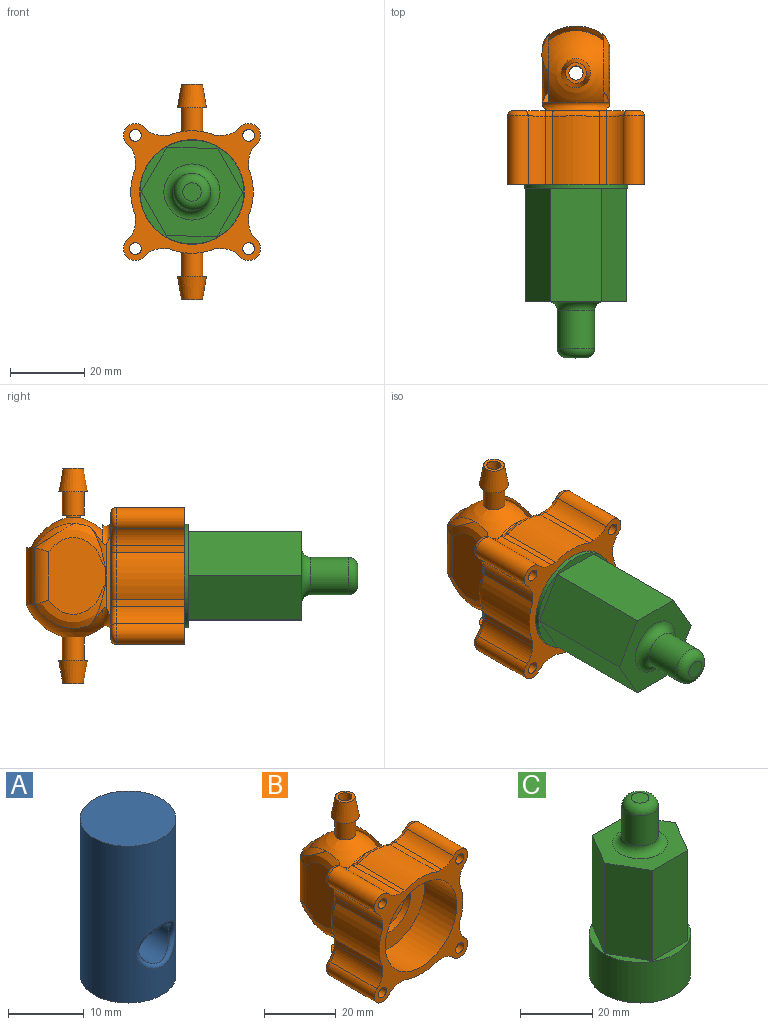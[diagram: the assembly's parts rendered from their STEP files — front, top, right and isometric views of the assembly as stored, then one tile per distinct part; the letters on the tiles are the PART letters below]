
ASSEMBLY  parts=3 mates=2
PART A: 6 faces, bbox 12.7x12.7x25.4 mm
  f0: cylinder r=6.35mm len=25.4mm, axis (0,0,-1), area 929.3mm2, adj f1,f2,f4,f5
  f1: plane 12.7x12.7mm, normal (0,0,1), area 126.7mm2, adj f0
  f2: plane 12.7x12.7mm, normal (0,0,-1), area 126.7mm2, adj f0
  f3: cylinder r=2.92mm len=11.68mm, axis (0,-1,0), area 194.6mm2, adj f4,f5
  f4: bspline ~7.46x6.86mm, area 19.4mm2, adj f0,f3
  f5: bspline ~7.46x6.86mm, area 19.4mm2, adj f0,f3
PART B: 95 faces, bbox 37.6x42.9x58.4 mm
  f0: cylinder r=16.51mm len=18.42mm, axis (0,-1,0), area 240.1mm2, adj f54,f56,f74,f94
  f1: cylinder r=16.51mm len=18.42mm, axis (0,-1,0), area 240.1mm2, adj f46,f52,f86,f94
  f2: cylinder r=16.51mm len=18.42mm, axis (0,-1,0), area 240.1mm2, adj f48,f58,f73,f94
  f3: cylinder r=11.43mm len=15.24mm, axis (0,0,-1), area 31.2mm2, adj f10,f11,f12,f13,f31,f33
  f4: cylinder r=11.43mm len=15.24mm, axis (0,0,-1), area 31.2mm2, adj f10,f11,f12,f13,f31,f35
  f5: cylinder r=11.43mm len=15.24mm, axis (0,0,-1), area 243.1mm2, adj f10,f11,f33,f35
  f6: revolved ~25.4x25.4mm, area 358.1mm2, adj f7,f19,f36,f37,f42,f43,f92
  f7: cylinder r=12.7mm len=15.24mm, axis (0,0,-1), area 238.7mm2, adj f6,f9,f38,f40
  f8: cylinder r=12.7mm len=24.07mm, axis (0,0,-1), area 39.5mm2, adj f25,f43,f92,f93
  f9: revolved ~25.4x25.4mm, area 358.2mm2, adj f7,f20,f37,f39,f41,f43,f93
  f10: revolved ~22.86x22.86mm, area 394.4mm2, adj f3,f4,f5,f12,f24,f33,f35
  f11: revolved ~22.86x22.86mm, area 394.4mm2, adj f3,f4,f5,f13,f15,f33,f35
  f12: plane 10.48x5.92mm, normal (0,1,0), area 35.4mm2, adj f3,f4,f10,f31
  f13: plane 10.48x5.92mm, normal (0,1,0), area 35.4mm2, adj f3,f4,f11,f31
  f14: cylinder r=12.7mm len=24.07mm, axis (0,0,-1), area 39.5mm2, adj f25,f37,f92,f93
  f15: cylinder r=1.91mm len=13.34mm, axis (0,0,-1), area 159.6mm2, adj f11,f16
  f16: plane 5.59x5.59mm, normal (0,0,-1), area 13.1mm2, adj f15,f17
  f17: cone r=2.79mm half-angle=10deg, axis (0,0,1), area 136mm2, adj f16,f18
  f18: plane 7.83x7.83mm, normal (0,0,1), area 21.4mm2, adj f17,f19
  f19: cylinder r=2.92mm len=6.35mm, axis (0,0,-1), area 116.5mm2, adj f6,f18
  f20: cylinder r=2.92mm len=6.35mm, axis (0,0,-1), area 116.5mm2, adj f9,f21
  f21: plane 7.83x7.83mm, normal (0,0,-1), area 21.4mm2, adj f20,f22
  f22: cone r=2.79mm half-angle=10deg, axis (0,0,-1), area 136mm2, adj f21,f23
  f23: plane 5.59x5.59mm, normal (0,0,1), area 13.1mm2, adj f22,f24
  f24: cylinder r=1.91mm len=13.34mm, axis (0,0,-1), area 159.6mm2, adj f10,f23
  f25: plane 34.04x34.04mm, normal (0,1,0), area 422mm2, adj f8,f14,f47,f51,f55,f59,f68,f69
  f26: cylinder r=16.51mm len=18.42mm, axis (0,-1,0), area 240.1mm2, adj f44,f50,f85,f94
  f27: cylinder r=14.1mm len=28.19mm, axis (0,-1,0), area 1124.9mm2, adj f28,f94
  f28: plane 28.19x28.19mm, normal (0,-1,0), area 390mm2, adj f27,f29
  f29: cylinder r=8.64mm len=17.27mm, axis (0,-1,0), area 117.2mm2, adj f28,f30
  f30: plane 17.27x17.27mm, normal (0,-1,0), area 102.5mm2, adj f29,f31
  f31: cylinder r=6.48mm len=12.95mm, axis (0,-1,0), area 201.6mm2, adj f3,f4,f12,f13,f30
  f32: plane 20.96x15.57mm, normal (-1,0,0), area 260mm2, adj f40,f41,f42,f43
  f33: plane 25.55x17.52mm, normal (1,0,0), area 392.3mm2, adj f3,f5,f10,f11
  f34: plane 20.95x15.57mm, normal (1,0,0), area 260mm2, adj f36,f37,f38,f39
  f35: plane 25.55x17.52mm, normal (-1,0,0), area 392.3mm2, adj f4,f5,f10,f11
  f36: bspline ~23.29x12.11mm, area 89mm2, adj f6,f34,f37,f38
  f37: cylinder r=5.08mm len=25.86mm, axis (0,0,-1), area 16.6mm2, adj f6,f9,f14,f34,f36,f39,f92,f93
  f38: cylinder r=5.08mm len=15.24mm, axis (0,0,-1), area 61.2mm2, adj f7,f34,f36,f39
  f39: bspline ~23.54x12.63mm, area 89mm2, adj f9,f34,f37,f38
  f40: cylinder r=5.08mm len=15.24mm, axis (0,0,-1), area 61.2mm2, adj f7,f32,f41,f42
  f41: bspline ~23.54x12.63mm, area 89mm2, adj f9,f32,f40,f43
  f42: bspline ~23.29x12.11mm, area 89mm2, adj f6,f32,f40,f43
  f43: cylinder r=5.08mm len=25.86mm, axis (0,0,-1), area 16.5mm2, adj f6,f8,f9,f32,f41,f42,f92,f93
  f44: plane 18.42x1.79mm, normal (0,0,-1), area 33mm2, adj f26,f62,f87,f94
  f45: cylinder r=3.17mm len=18.42mm, axis (0,-1,0), area 190.2mm2, adj f62,f63,f91,f94
  f46: plane 18.42x1.79mm, normal (1,0,0), area 33mm2, adj f1,f63,f88,f94
  f47: cylinder r=1.59mm len=19.81mm, axis (0,-1,0), area 197.6mm2, adj f25,f94
  f48: plane 18.42x1.79mm, normal (-1,0,0), area 33mm2, adj f2,f61,f75,f94
  f49: cylinder r=3.17mm len=18.42mm, axis (0,-1,0), area 190.2mm2, adj f60,f61,f79,f94
  f50: plane 18.42x1.79mm, normal (0,0,-1), area 33mm2, adj f26,f60,f83,f94
  f51: cylinder r=1.59mm len=19.81mm, axis (0,-1,0), area 197.6mm2, adj f25,f94
  f52: plane 18.42x1.79mm, normal (1,0,0), area 33mm2, adj f1,f64,f84,f94
  f53: cylinder r=3.17mm len=18.42mm, axis (0,-1,0), area 190.2mm2, adj f64,f65,f80,f94
  f54: plane 18.42x1.79mm, normal (0,0,1), area 33mm2, adj f0,f65,f76,f94
  f55: cylinder r=1.59mm len=19.81mm, axis (0,-1,0), area 197.6mm2, adj f25,f94
  f56: plane 18.42x1.79mm, normal (0,0,1), area 33mm2, adj f0,f67,f72,f94
  f57: cylinder r=3.17mm len=18.42mm, axis (0,-1,0), area 190.2mm2, adj f66,f67,f68,f94
  f58: plane 18.42x1.79mm, normal (-1,0,0), area 33mm2, adj f2,f66,f71,f94
  f59: cylinder r=1.59mm len=19.81mm, axis (0,-1,0), area 197.6mm2, adj f25,f94
  f60: cylinder r=6.35mm len=18.42mm, axis (0,-1,0), area 98.4mm2, adj f49,f50,f81,f94
  f61: cylinder r=6.35mm len=18.42mm, axis (0,-1,0), area 98.4mm2, adj f48,f49,f77,f94
  f62: cylinder r=6.35mm len=18.42mm, axis (0,-1,0), area 98.4mm2, adj f44,f45,f89,f94
  f63: cylinder r=6.35mm len=18.42mm, axis (0,-1,0), area 98.4mm2, adj f45,f46,f90,f94
  f64: cylinder r=6.35mm len=18.42mm, axis (0,-1,0), area 98.4mm2, adj f52,f53,f82,f94
  f65: cylinder r=6.35mm len=18.42mm, axis (0,-1,0), area 98.4mm2, adj f53,f54,f78,f94
  f66: cylinder r=6.35mm len=18.42mm, axis (0,-1,0), area 98.4mm2, adj f57,f58,f69,f94
  f67: cylinder r=6.35mm len=18.42mm, axis (0,-1,0), area 98.4mm2, adj f56,f57,f70,f94
  f68: torus R=1.78mm, axis (0,-1,0), area 19mm2, adj f25,f57,f69,f70
  f69: torus R=7.75mm, axis (0,-1,0), area 12.7mm2, adj f25,f66,f68,f71
  f70: torus R=7.75mm, axis (0,-1,0), area 12.7mm2, adj f25,f67,f68,f72
  f71: cylinder r=1.4mm len=2.08mm, axis (0,0,1), area 4.2mm2, adj f25,f58,f69,f73
  f72: cylinder r=1.4mm len=2.08mm, axis (1,0,0), area 4.2mm2, adj f25,f56,f70,f74
  f73: torus R=15.11mm, axis (0,-1,0), area 28.4mm2, adj f2,f25,f71,f75
  f74: torus R=15.11mm, axis (0,-1,0), area 28.4mm2, adj f0,f25,f72,f76
  f75: cylinder r=1.4mm len=2.08mm, axis (0,0,1), area 4.2mm2, adj f25,f48,f73,f77
  f76: cylinder r=1.4mm len=2.08mm, axis (1,0,0), area 4.2mm2, adj f25,f54,f74,f78
  f77: torus R=7.75mm, axis (0,-1,0), area 12.7mm2, adj f25,f61,f75,f79
  f78: torus R=7.75mm, axis (0,-1,0), area 12.7mm2, adj f25,f65,f76,f80
  f79: torus R=1.78mm, axis (0,-1,0), area 19mm2, adj f25,f49,f77,f81
  f80: torus R=1.78mm, axis (0,-1,0), area 19mm2, adj f25,f53,f78,f82
  f81: torus R=7.75mm, axis (0,-1,0), area 12.7mm2, adj f25,f60,f79,f83
  f82: torus R=7.75mm, axis (0,-1,0), area 12.7mm2, adj f25,f64,f80,f84
  f83: cylinder r=1.4mm len=2.08mm, axis (-1,0,0), area 4.2mm2, adj f25,f50,f81,f85
  f84: cylinder r=1.4mm len=2.08mm, axis (0,0,-1), area 4.2mm2, adj f25,f52,f82,f86
  f85: torus R=15.11mm, axis (0,-1,0), area 28.4mm2, adj f25,f26,f83,f87
  f86: torus R=15.11mm, axis (0,-1,0), area 28.4mm2, adj f1,f25,f84,f88
  f87: cylinder r=1.4mm len=2.08mm, axis (-1,0,0), area 4.2mm2, adj f25,f44,f85,f89
  f88: cylinder r=1.4mm len=2.08mm, axis (0,0,-1), area 4.2mm2, adj f25,f46,f86,f90
  f89: torus R=7.75mm, axis (0,-1,0), area 12.7mm2, adj f25,f62,f87,f91
  f90: torus R=7.75mm, axis (0,-1,0), area 12.7mm2, adj f25,f63,f88,f91
  f91: torus R=1.78mm, axis (0,-1,0), area 19mm2, adj f25,f45,f89,f90
  f92: bspline ~22.01x8.22mm, area 61mm2, adj f6,f8,f14,f25,f37,f43
  f93: bspline ~22.01x8.22mm, area 61mm2, adj f8,f9,f14,f25,f37,f43
  f94: plane 36.83x36.83mm, normal (0,-1,0), area 426.7mm2, adj f0,f1,f2,f26,f27,f44,f45,f46
PART C: 14 faces, bbox 28x28x59.4 mm
  f0: plane 27.99x27.99mm, normal (0,0,1), area 128.4mm2, adj f1,f3,f4,f5,f6,f7,f8
  f1: cylinder r=14mm len=27.99mm, axis (0,0,-1), area 1206.1mm2, adj f0,f2
  f2: plane 27.99x27.99mm, normal (0,0,-1), area 615.3mm2, adj f1
  f3: plane 30.48x11.88mm, normal (-0.87,-0.5,0), area 417.3mm2, adj f0,f4,f8,f9
  f4: plane 30.48x13.69mm, normal (0,-1,0), area 417.3mm2, adj f0,f3,f5,f9
  f5: plane 30.48x11.83mm, normal (0.86,-0.5,0), area 417.3mm2, adj f0,f4,f6,f9
  f6: plane 30.48x11.88mm, normal (0.87,0.5,0), area 417.3mm2, adj f0,f5,f7,f9
  f7: plane 30.48x13.69mm, normal (0,1,0), area 417.3mm2, adj f0,f6,f8,f9
  f8: plane 30.48x11.83mm, normal (-0.86,0.5,0), area 417.3mm2, adj f0,f3,f7,f9
  f9: plane 27.38x23.77mm, normal (0,0,1), area 307.4mm2, adj f3,f4,f5,f6,f7,f8,f12
  f10: cylinder r=5.02mm len=10.16mm, axis (0,0,-1), area 320.4mm2, adj f12,f13
  f11: plane 4.96x4.96mm, normal (0,0,1), area 19.3mm2, adj f13
  f12: torus R=7.56mm, axis (0,0,1), area 149mm2, adj f9,f10
  f13: torus R=2.48mm, axis (0,0,1), area 102.7mm2, adj f10,f11
PLACE A rot(axis=(1,0,0),90deg) t=(0.34,8.05,0.35)mm
PLACE B t=(0.34,-0.08,0.35)mm
PLACE C rot(axis=(1,0,0),90deg) t=(0.34,8.05,0.35)mm
MATE fastened A.f0 <-> B.f0  axis (0,-1,0) through (0.34,-17.35,0.35)mm
MATE fastened C.f1 <-> A.f0  axis (0,1,0) through (0.34,-17.35,0.35)mm
